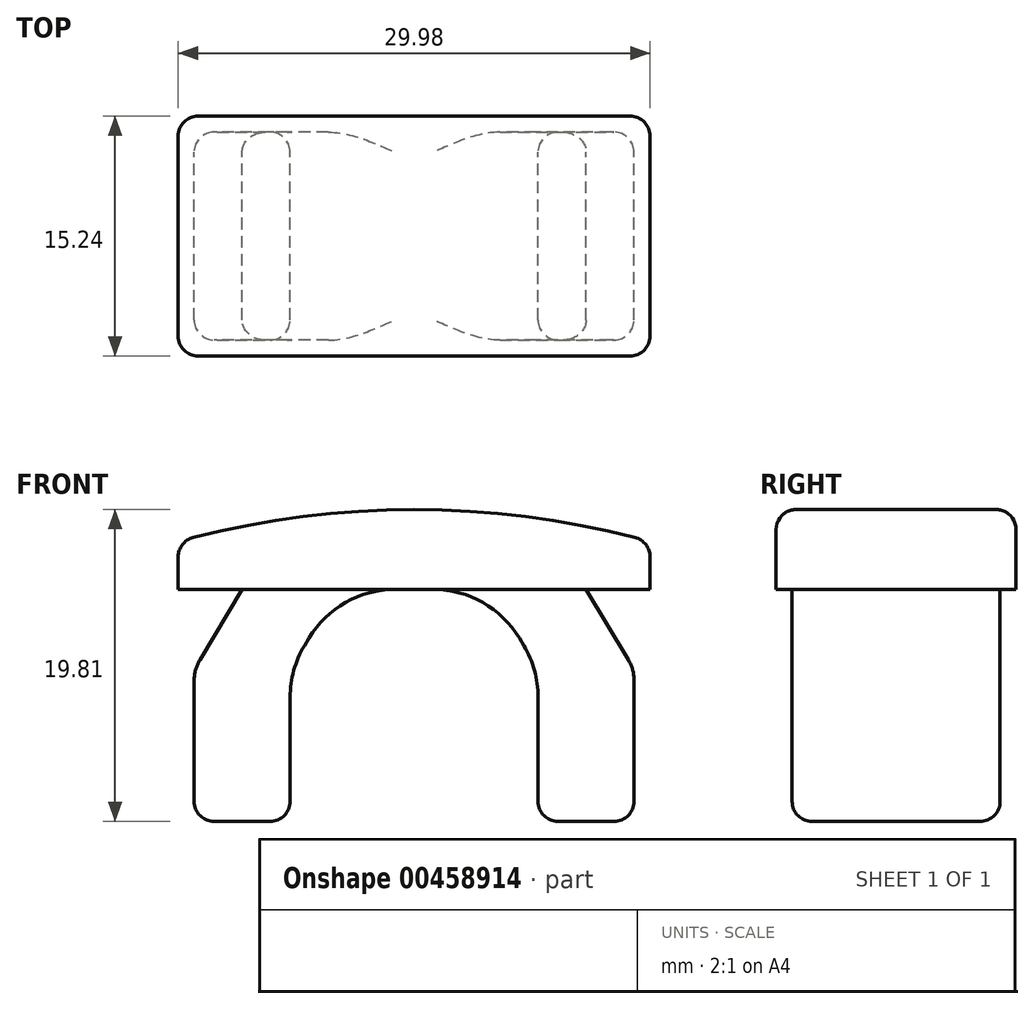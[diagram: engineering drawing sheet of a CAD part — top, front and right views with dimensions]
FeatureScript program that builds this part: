
annotation { "Feature Type Name" : "Feature", "Feature Type Description" : "" }
export const myFeature = defineFeature(function(context is Context, id is Id, definition is map)
    precondition{}
    {
        {
            var Q0;
            Q0=qCreatedBy(makeId("Front.planeOp"),FACE);
            var sketch = newSketch(context, id + "F0", { "sketchPlane" : qUnion([Q0])});
            skLineSegment(sketch, "E0", {"start": v(0, 0) * mm, "end": v(14.99, 0) * mm});
            skLineSegment(sketch, "E1", {"start": v(14.99, 0) * mm, "end": v(-14.99, 0) * mm});
            skLineSegment(sketch, "E2", {"start": v(-14.99, 0) * mm, "end": v(-14.99, 3.05) * mm});
            skLineSegment(sketch, "E3", {"start": v(14.99, 3.05) * mm, "end": v(14.99, 0) * mm});
            skPoint(sketch, "E4.endSnap0", {"position": v(0, 3.05) * mm});
            skArc(sketch, "E5", {"start": v(14.99, 3.05) * mm, "mid": v(0, 5.08) * mm, "end": v(-14.99, 3.05) * mm});
            skPoint(sketch, "E6.orphan", {"position": v(0, 5.08) * mm});
            skSolve(sketch);
        }
        {
            var Q0;
            Q0 = qSketchRegion(id + "F0", true);
            extrude(context, id + "F1", {"entities" : qUnion([Q0]), "endBound" : BoundingType.SYMMETRIC, "depth" : 15.24 * mm});
        }
        {
            var Q0;
            Q0=qCreatedBy(makeId("Front.planeOp"),FACE);
            var sketch = newSketch(context, id + "F2", { "sketchPlane" : qUnion([Q0])});
            skLineSegment(sketch, "E7", {"start": v(-9.14, -14.73) * mm, "end": v(-12.7, -14.73) * mm});
            skLineSegment(sketch, "E8", {"start": v(-13.97, -13.46) * mm, "end": v(-13.97, -5.78) * mm});
            skLineSegment(sketch, "E9", {"start": v(-1.23, 0) * mm, "end": v(0, 0) * mm});
            skLineSegment(sketch, "E10", {"start": v(-13.6, -4.48) * mm, "end": v(-10.92, 0) * mm});
            skPoint(sketch, "E11.orphan", {"position": v(13.97, 0) * mm});
            skLineSegment(sketch, "E12.0", {"start": v(-7.87, -13.46) * mm, "end": v(-7.87, -6.84) * mm});
            skLineSegment(sketch, "E13", {"start": v(-6.97, -3.57) * mm, "end": v(-6.68, -3.08) * mm});
            skPoint(sketch, "E14.newPointB", {"position": v(-13.97, 0) * mm});
            skArc(sketch, "E14.filletArc", {"start": v(-1.23, 0) * mm, "mid": v(-4.36, -0.82) * mm, "end": v(-6.68, -3.08) * mm});
            skLineSegment(sketch, "E15", {"start": v(0, 0) * mm, "end": v(0, -14.73) * mm, "construction": true});
            skPoint(sketch, "E16.end.orphan", {"position": v(4.83, 0) * mm});
            skPoint(sketch, "E17.end.orphan", {"position": v(10.92, 0) * mm});
            skPoint(sketch, "E18.visualSharp", {"position": v(-7.87, -5.08) * mm});
            skArc(sketch, "E18.filletArc", {"start": v(-6.97, -3.57) * mm, "mid": v(-7.64, -5.14) * mm, "end": v(-7.87, -6.84) * mm});
            skPoint(sketch, "E19.visualSharp", {"position": v(-7.87, -14.73) * mm});
            skArc(sketch, "E19.filletArc", {"start": v(-9.14, -14.73) * mm, "mid": v(-8.25, -14.36) * mm, "end": v(-7.87, -13.46) * mm});
            skPoint(sketch, "E20.visualSharp", {"position": v(-13.97, -14.73) * mm});
            skArc(sketch, "E20.filletArc", {"start": v(-13.97, -13.46) * mm, "mid": v(-13.6, -14.36) * mm, "end": v(-12.7, -14.73) * mm});
            skPoint(sketch, "E21.visualSharp", {"position": v(-13.97, -5.08) * mm});
            skArc(sketch, "E21.filletArc", {"start": v(-13.6, -4.48) * mm, "mid": v(-13.88, -5.1) * mm, "end": v(-13.97, -5.78) * mm});
            skPoint(sketch, "E22.0", {"position": v(-14.99, 0) * mm});
            skLineSegment(sketch, "E23", {"start": v(0, 0) * mm, "end": v(-10.92, 0) * mm});
            skLineSegment(sketch, "E24.MirrorCS", {"start": v(6.97, -3.57) * mm, "end": v(6.68, -3.08) * mm});
            skArc(sketch, "E25.MirrorCS", {"start": v(13.6, -4.48) * mm, "mid": v(13.88, -5.1) * mm, "end": v(13.97, -5.78) * mm});
            skArc(sketch, "E26.MirrorCS", {"start": v(9.14, -14.73) * mm, "mid": v(8.25, -14.36) * mm, "end": v(7.87, -13.46) * mm});
            skArc(sketch, "E27.MirrorCS", {"start": v(13.97, -13.46) * mm, "mid": v(13.6, -14.36) * mm, "end": v(12.7, -14.73) * mm});
            skArc(sketch, "E28.MirrorCS", {"start": v(1.23, 0) * mm, "mid": v(4.36, -0.82) * mm, "end": v(6.68, -3.08) * mm});
            skLineSegment(sketch, "E29.MirrorCS", {"start": v(7.87, -13.46) * mm, "end": v(7.87, -6.84) * mm});
            skArc(sketch, "E30.MirrorCS", {"start": v(6.97, -3.57) * mm, "mid": v(7.64, -5.14) * mm, "end": v(7.87, -6.84) * mm});
            skLineSegment(sketch, "E31.MirrorCS", {"start": v(9.14, -14.73) * mm, "end": v(12.7, -14.73) * mm});
            skPoint(sketch, "E32.MirrorP", {"position": v(7.87, -14.73) * mm});
            skLineSegment(sketch, "E33.MirrorCS", {"start": v(13.6, -4.48) * mm, "end": v(10.92, 0) * mm});
            skLineSegment(sketch, "E34.MirrorCS", {"start": v(13.97, -13.46) * mm, "end": v(13.97, -5.78) * mm});
            skPoint(sketch, "E35.MirrorP", {"position": v(14.99, 0) * mm});
            skPoint(sketch, "E36.MirrorP", {"position": v(13.97, -14.73) * mm});
            skPoint(sketch, "E37.MirrorP", {"position": v(7.87, -5.08) * mm});
            skPoint(sketch, "E38.MirrorP", {"position": v(13.97, -5.08) * mm});
            skLineSegment(sketch, "E39", {"start": v(1.23, 0) * mm, "end": v(10.92, 0) * mm});
            skSolve(sketch);
        }
        {
            var Q0;
            Q0 = qSketchRegion(id + "F2", true);
            extrude(context, id + "F3", {"entities" : qUnion([Q0]), "operationType" : NewBodyOperationType.ADD, "endBound" : BoundingType.SYMMETRIC, "depth" : 13.2 * mm});
        }
        {
            var Q0;
            Q0=makeQuery(id+"F1.opExtrude","CAP_EDGE",EDGE,{"disambiguationData":[OSD([sQuery(id+"F0.wireOp",EDGE,"E5")])],"isStart":false});
            var Q1;
            Q1=makeQuery(id+"F1.opExtrude","CAP_EDGE",EDGE,{"disambiguationData":[OSD([sQuery(id+"F0.wireOp",EDGE,"E5")])],"isStart":true});
            var Q2;
            Q2=makeQuery(id+"F1.opExtrude","SWEPT_EDGE",EDGE,{"disambiguationData":[OSD([sQuery(id+"F0.wireOp",EDGE,"E2"),sQuery(id+"F0.wireOp",EDGE,"E5")])]});
            var Q3;
            Q3=makeQuery(id+"F1.opExtrude","CAP_EDGE",EDGE,{"disambiguationData":[OSD([sQuery(id+"F0.wireOp",EDGE,"E2")])],"isStart":false});
            var Q4;
            Q4=makeQuery(id+"F1.opExtrude","CAP_EDGE",EDGE,{"disambiguationData":[OSD([sQuery(id+"F0.wireOp",EDGE,"E3")])],"isStart":false});
            var Q5;
            Q5=makeQuery(id+"F1.opExtrude","SWEPT_EDGE",EDGE,{"disambiguationData":[OSD([sQuery(id+"F0.wireOp",EDGE,"E3"),sQuery(id+"F0.wireOp",EDGE,"E5")])]});
            var Q6;
            Q6=makeQuery(id+"F1.opExtrude","CAP_EDGE",EDGE,{"disambiguationData":[OSD([sQuery(id+"F0.wireOp",EDGE,"E3")])],"isStart":true});
            var Q7;
            Q7=makeQuery(id+"F1.opExtrude","CAP_EDGE",EDGE,{"disambiguationData":[OSD([sQuery(id+"F0.wireOp",EDGE,"E2")])],"isStart":true});
            var Q8;
            Q8=makeQuery(id+"F3.opExtrude","CAP_EDGE",EDGE,{"disambiguationData":[OSD([sQuery(id+"F2.wireOp",EDGE,"E18.filletArc")])],"isStart":true});
            var Q9;
            Q9=makeQuery(id+"F3.opExtrude","CAP_EDGE",EDGE,{"disambiguationData":[OSD([sQuery(id+"F2.wireOp",EDGE,"E30.MirrorCS")])],"isStart":true});
            var Q10;
            Q10=makeQuery(id+"F3.opExtrude","CAP_EDGE",EDGE,{"disambiguationData":[OSD([sQuery(id+"F2.wireOp",EDGE,"E30.MirrorCS")])],"isStart":false});
            var Q11;
            Q11=makeQuery(id+"F3.opExtrude","CAP_EDGE",EDGE,{"disambiguationData":[OSD([sQuery(id+"F2.wireOp",EDGE,"E18.filletArc")])],"isStart":false});
            fillet(context, id + "F4", {"entities" : qUnion([Q0, Q1, Q2, Q3, Q4, Q5, Q6, Q7, Q8, Q9, Q10, Q11]), "radius" : 1.27 * mm, "tangentPropagation" : true, "allowEdgeOverflow" : false});
        }
    });
